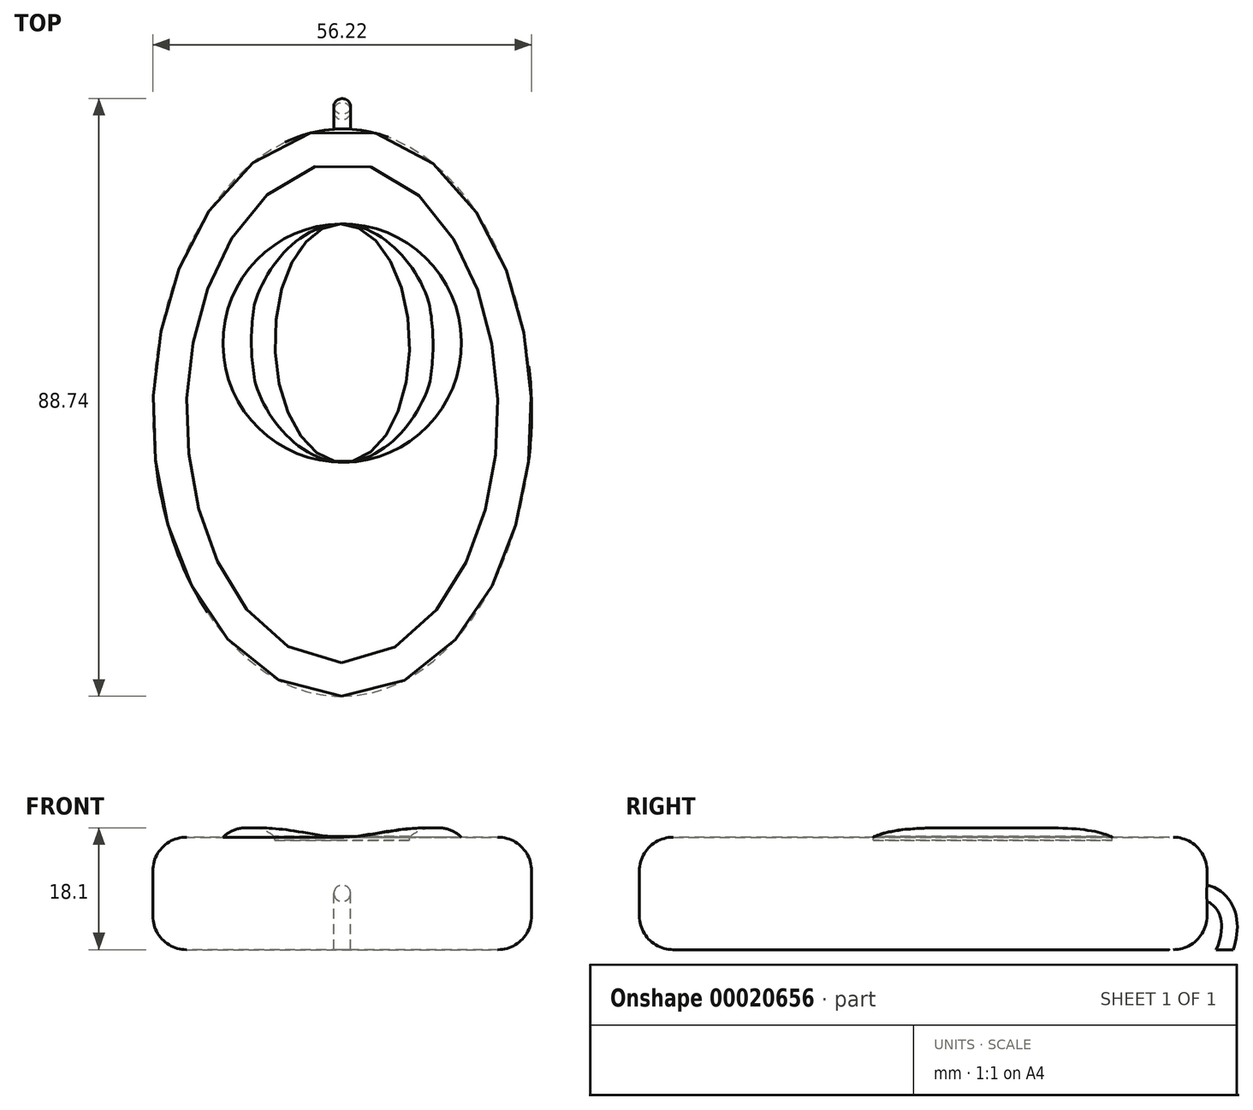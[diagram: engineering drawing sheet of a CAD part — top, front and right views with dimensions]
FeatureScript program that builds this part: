
annotation { "Feature Type Name" : "Feature", "Feature Type Description" : "" }
export const myFeature = defineFeature(function(context is Context, id is Id, definition is map)
    precondition{}
    {
        {
            var Q0;
            Q0=qCreatedBy(makeId("Top.planeOp"),FACE);
            var sketch = newSketch(context, id + "F0", { "sketchPlane" : qUnion([Q0])});
            skEllipse(sketch, "E0", {"center": v(0, 0) * mm, "majorRadius": 42.12 * mm, "minorRadius": 28.1 * mm, "majorAxis": v(0, -1)});
            skPoint(sketch, "E1", {"position": v(0, 42.12) * mm});
            skSolve(sketch);
        }
        {
            var Q0;
            Q0=makeQuery(id+"F0.imprint","IMPRINT",FACE,{"disambiguationData":[TD([[makeQuery(id+"F0.imprint","IMPRINT",EDGE,{"derivedFrom":sQuery(id+"F0.wireOp",EDGE,"E0")}),1.0]])]});
            extrude(context, id + "F1", {"entities" : qUnion([Q0]), "depth" : 16.7 * mm});
        }
        {
            var Q0;
            Q0=makeQuery(id+"F1.opExtrude","CAP_FACE",FACE,{"disambiguationData":[OSD([sQuery(id+"F0.wireOp",EDGE,"E0")])],"isStart":true});
            var Q1;
            Q1=makeQuery(id+"F1.opExtrude","CAP_FACE",FACE,{"disambiguationData":[OSD([sQuery(id+"F0.wireOp",EDGE,"E0")])],"isStart":false});
            fillet(context, id + "F2", {"entities" : qUnion([Q0, Q1]), "radius" : 5 * mm, "tangentPropagation" : true, "allowEdgeOverflow" : false});
        }
        {
            var Q0;
            Q0=makeQuery(id+"F1.opExtrude","CAP_FACE",FACE,{"disambiguationData":[OSD([sQuery(id+"F0.wireOp",EDGE,"E0")])],"isStart":false});
            var sketch = newSketch(context, id + "F3", { "sketchPlane" : qUnion([Q0])});
            skCircle(sketch, "E2", {"center": v(0, 10.32) * mm, "radius": 17.7 * mm});
            skEllipse(sketch, "E3", {"center": v(0, 10.32) * mm, "majorRadius": 17.7 * mm, "minorRadius": 10 * mm, "majorAxis": v(-0.01, 1)});
            skPoint(sketch, "E4", {"position": v(0, 28.02) * mm});
            skLineSegment(sketch, "E5", {"start": v(0, 33.14) * mm, "end": v(0, -15.75) * mm, "construction": true});
            skPoint(sketch, "E6", {"position": v(0, -7.38) * mm});
            skSolve(sketch);
        }
        {
            var Q0;
            {var subQ0=sQuery(id+"F3.wireOp",EDGE,"E3");var subQ1=sQuery(id+"F3.wireOp",EDGE,"E2");var subQ3=makeQuery(id+"F3.imprint","INTERSECT",VERTEX,{"disambiguationData":[OD(0.0)],"derivedFrom":[subQ1,subQ0]});Q0=makeQuery(id+"F3.imprint","IMPRINT",FACE,{"disambiguationData":[TD([[makeQuery(id+"F3.imprint","IMPRINT",EDGE,{"disambiguationData":[TD([[subQ3,1.0]])],"derivedFrom":subQ0}),1.0]])]});}
            extrude(context, id + "F4", {"entities" : qUnion([Q0]), "operationType" : NewBodyOperationType.REMOVE, "oppositeDirection" : true, "depth" : 0.5 * mm});
        }
        {
            var Q0;
            {var subQ0=sQuery(id+"F3.wireOp",EDGE,"E3");var subQ1=sQuery(id+"F3.wireOp",EDGE,"E2");var subQ3=makeQuery(id+"F3.imprint","INTERSECT",VERTEX,{"disambiguationData":[OD(0.0)],"derivedFrom":[subQ1,subQ0]});Q0=makeQuery(id+"F3.imprint","IMPRINT",FACE,{"disambiguationData":[TD([[makeQuery(id+"F3.imprint","IMPRINT",EDGE,{"disambiguationData":[TD([[subQ3,-1.0]])],"derivedFrom":subQ1}),1.0]])]});}
            var Q1;
            {var subQ0=sQuery(id+"F3.wireOp",EDGE,"E3");var subQ1=sQuery(id+"F3.wireOp",EDGE,"E2");var subQ3=makeQuery(id+"F3.imprint","INTERSECT",VERTEX,{"disambiguationData":[OD(0.0)],"derivedFrom":[subQ1,subQ0]});Q1=makeQuery(id+"F3.imprint","IMPRINT",FACE,{"disambiguationData":[TD([[makeQuery(id+"F3.imprint","IMPRINT",EDGE,{"disambiguationData":[TD([[subQ3,1.0]])],"derivedFrom":subQ1}),1.0]])]});}
            extrude(context, id + "F5", {"entities" : qUnion([Q0, Q1]), "depth" : 1.4 * mm});
        }
        {
            var Q0;
            {var subQ0=sQuery(id+"F3.wireOp",EDGE,"E2");var subQ1=sQuery(id+"F3.wireOp",EDGE,"E3");var subQ3=makeQuery(id+"F3.imprint","INTERSECT",VERTEX,{"disambiguationData":[OD(0.0)],"derivedFrom":[subQ0,subQ1]});Q0=makeQuery(id+"F5.opExtrude","CAP_FACE",FACE,{"disambiguationData":[OSD([subQ0,subQ1]),TDD([makeQuery(id+"F3.imprint","IMPRINT",EDGE,{"disambiguationData":[TD([[subQ3,1.0]])],"derivedFrom":subQ0}),makeQuery(id+"F3.imprint","IMPRINT",EDGE,{"disambiguationData":[TD([[subQ3,1.0]])],"derivedFrom":subQ1})])],"isStart":false});}
            var Q1;
            {var subQ0=sQuery(id+"F3.wireOp",EDGE,"E2");var subQ1=sQuery(id+"F3.wireOp",EDGE,"E3");var subQ3=makeQuery(id+"F3.imprint","INTERSECT",VERTEX,{"disambiguationData":[OD(0.0)],"derivedFrom":[subQ0,subQ1]});Q1=makeQuery(id+"F5.opExtrude","CAP_FACE",FACE,{"disambiguationData":[OSD([subQ0,subQ1]),TDD([makeQuery(id+"F3.imprint","IMPRINT",EDGE,{"disambiguationData":[TD([[subQ3,-1.0]])],"derivedFrom":subQ0}),makeQuery(id+"F3.imprint","IMPRINT",EDGE,{"disambiguationData":[TD([[subQ3,-1.0]])],"derivedFrom":subQ1})])],"isStart":false});}
            fillet(context, id + "F6", {"entities" : qUnion([Q0, Q1]), "radius" : 5 * mm, "tangentPropagation" : true, "allowEdgeOverflow" : false});
        }
        {
            var Q0;
            Q0=qCreatedBy(makeId("Right.planeOp"),FACE);
            var sketch = newSketch(context, id + "F7", { "sketchPlane" : qUnion([Q0])});
            skFitSpline(sketch, "E7", {"points": [v(44.75, 0) * mm, v(42.12, 8.35) * mm, v(38.53, 8.1) * mm], "startDerivative": vector(9.27, 24.23) * mm, "endDerivative": vector(-6.7, -0.05) * mm});
            skLineSegment(sketch, "E8", {"start": v(42.12, 5) * mm, "end": v(42.12, 11.7) * mm, "construction": true});
            skSolve(sketch);
        }
        {
            var Q0;
            Q0=qCreatedBy(makeId("Top.planeOp"),FACE);
            var sketch = newSketch(context, id + "F8", { "sketchPlane" : qUnion([Q0])});
            skCircle(sketch, "E9", {"center": v(0, 24.08) * mm, "radius": 1 * mm});
            skCircle(sketch, "E10", {"center": v(0, 44.75) * mm, "radius": 1.25 * mm});
            skSolve(sketch);
        }
        {
            var Q0;
            Q0=makeQuery(id+"F8.imprint","IMPRINT",FACE,{"disambiguationData":[TD([[makeQuery(id+"F8.imprint","IMPRINT",EDGE,{"derivedFrom":sQuery(id+"F8.wireOp",EDGE,"E10")}),1.0]])]});
            var Q1;
            Q1=sQuery(id+"F7.wireOp",EDGE,"E7");
            sweep(context, id + "F9", {"operationType" : NewBodyOperationType.ADD, "profiles" : qUnion([Q0]), "path" : qUnion([Q1])});
        }
        {
            var Q0;
            {var subQ0=sQuery(id+"F3.wireOp",EDGE,"E3");var subQ1=sQuery(id+"F3.wireOp",EDGE,"E2");var subQ3=makeQuery(id+"F3.imprint","INTERSECT",VERTEX,{"disambiguationData":[OD(0.0)],"derivedFrom":[subQ1,subQ0]});Q0=makeQuery(id+"F3.imprint","IMPRINT",FACE,{"disambiguationData":[TD([[makeQuery(id+"F3.imprint","IMPRINT",EDGE,{"disambiguationData":[TD([[subQ3,1.0]])],"derivedFrom":subQ0}),1.0]])]});}
            extrude(context, id + "F10", {"entities" : qUnion([Q0]), "depth" : 0.1 * mm});
        }
    });
